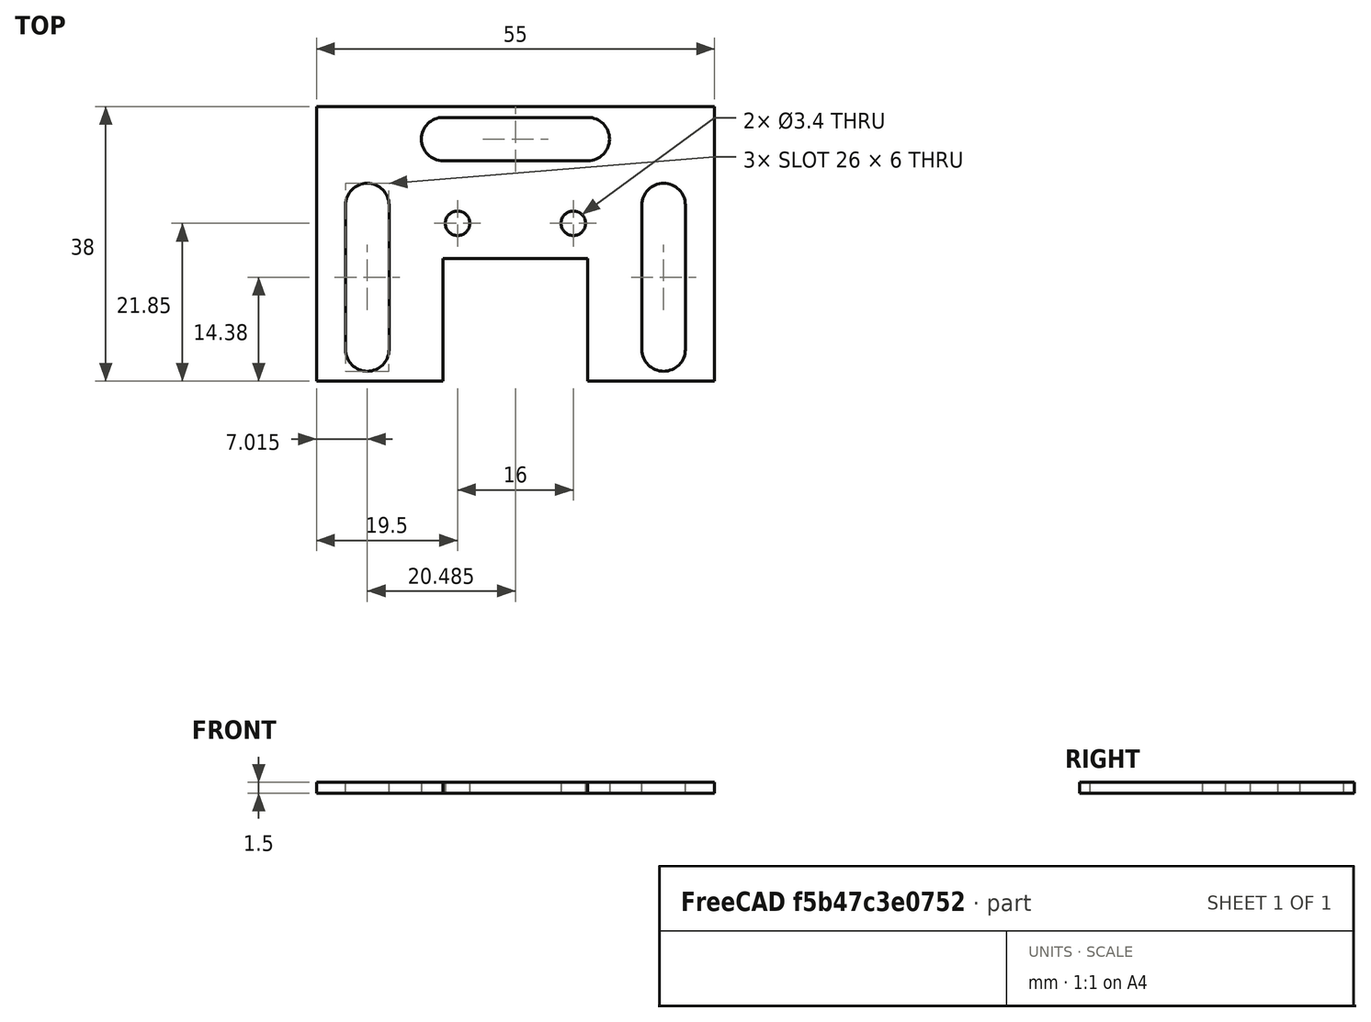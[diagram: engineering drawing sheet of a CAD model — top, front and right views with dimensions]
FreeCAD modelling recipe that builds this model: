
FCSTD DOCUMENT  (FreeCAD 0.18.4R)
Label: magnet_support_fixed_1.01
License: All rights reserved
LicenseURL: http://en.wikipedia.org/wiki/All_rights_reserved
objects: Sketcher::SketchObject×1, PartDesign::Pad×1, PartDesign::Body×1
note: 4 computed .brp shape members not serialized (recipe doc carries the construction recipe); baked Part::Feature solids carry a one-line shape summary decoded from their .brp

FEATURE [Sketcher::SketchObject] Sketch
  MapMode = 5
  Support = -> [XY_Plane]
  sketch-geometry (22):
    g0: LineSegment StartX=-27.5 StartY=19 StartZ=0 EndX=27.5 EndY=19 EndZ=0
    g1: LineSegment StartX=27.5 StartY=19 StartZ=0 EndX=27.5 EndY=-19 EndZ=0
    g2: LineSegment StartX=-27.5 StartY=-19 StartZ=0 EndX=-27.5 EndY=19 EndZ=0
    g3: Circle CenterX=-8 CenterY=2.85 CenterZ=0 NormalX=0 NormalY=0 NormalZ=1 AngleXU=0 Radius=1.7
    g4: Circle CenterX=8 CenterY=2.85 CenterZ=0 NormalX=0 NormalY=0 NormalZ=1 AngleXU=0 Radius=1.7
    g5: LineSegment StartX=-27.5 StartY=-19 StartZ=0 EndX=-10 EndY=-19 EndZ=0
    g6: LineSegment StartX=-10 StartY=-19 StartZ=0 EndX=-10 EndY=-2 EndZ=0
    g7: LineSegment StartX=-10 StartY=-2 StartZ=0 EndX=10 EndY=-2 EndZ=0
    g8: LineSegment StartX=10 StartY=-2 StartZ=0 EndX=10 EndY=-19 EndZ=0
    g9: LineSegment StartX=10 StartY=-19 StartZ=0 EndX=27.5 EndY=-19 EndZ=0
    g10: ArcOfCircle CenterX=-10 CenterY=14.5 CenterZ=0 NormalX=0 NormalY=0 NormalZ=1 AngleXU=0 Radius=3 StartAngle=1.5708 EndAngle=4.71239
    g11: ArcOfCircle CenterX=10 CenterY=14.5 CenterZ=0 NormalX=0 NormalY=0 NormalZ=1 AngleXU=0 Radius=3 StartAngle=4.71239 EndAngle=7.85398
    g12: LineSegment StartX=-10 StartY=11.5 StartZ=0 EndX=10 EndY=11.5 EndZ=0
    g13: LineSegment StartX=-10 StartY=17.5 StartZ=0 EndX=10 EndY=17.5 EndZ=0
    g14: ArcOfCircle CenterX=20.485 CenterY=5.38 CenterZ=0 NormalX=0 NormalY=0 NormalZ=1 AngleXU=0 Radius=3 StartAngle=1e-16 EndAngle=3.14159
    g15: ArcOfCircle CenterX=20.485 CenterY=-14.62 CenterZ=0 NormalX=0 NormalY=0 NormalZ=1 AngleXU=0 Radius=3 StartAngle=3.14159 EndAngle=6.28319
    g16: LineSegment StartX=17.485 StartY=5.38 StartZ=0 EndX=17.485 EndY=-14.62 EndZ=0
    g17: LineSegment StartX=23.485 StartY=5.38 StartZ=0 EndX=23.485 EndY=-14.62 EndZ=0
    g18: ArcOfCircle CenterX=-20.485 CenterY=-14.62 CenterZ=0 NormalX=0 NormalY=0 NormalZ=1 AngleXU=0 Radius=3 StartAngle=3.14159 EndAngle=6.28319
    g19: ArcOfCircle CenterX=-20.485 CenterY=5.38 CenterZ=0 NormalX=0 NormalY=0 NormalZ=1 AngleXU=0 Radius=3 StartAngle=0 EndAngle=3.14159
    g20: LineSegment StartX=-17.485 StartY=-14.62 StartZ=0 EndX=-17.485 EndY=5.38 EndZ=0
    g21: LineSegment StartX=-23.485 StartY=-14.62 StartZ=0 EndX=-23.485 EndY=5.38 EndZ=0
  constraints (54):
    c: Coincident(g0,g1)
    c: Coincident(g2,g0)
    c: Vertical(g1)
    c: DistanceX(g0,g0) = 55
    c: DistanceY(g2,g2) = 38
    c: Symmetric(g0,g0,g-2)
    c: Symmetric(g0,g2,g-1)
    c: Symmetric(g3,g4,g-2)
    c: Distance(g4,g3) = 16
    c: Coincident(g2,g5)
    c: Horizontal(g5)
    c: Coincident(g5,g6)
    c: Vertical(g6)
    c: Coincident(g6,g7)
    c: Coincident(g7,g8)
    c: Coincident(g8,g9)
    c: Coincident(g9,g1)
    c: Horizontal(g9)
    c: Horizontal(g5,g8)
    c: Vertical(g8,g7)
    c: DistanceX(g7,g7) = 20
    c: Symmetric(g6,g7,g-2)
    c: DistanceY(g6,g6) = 17
    c: Tangent(g10,g13) = 1.5708
    c: Tangent(g10,g12) = -1.5708
    c: Tangent(g12,g11) = -1.5708
    c: Tangent(g13,g11) = 1.5708
    c: Horizontal(g12)
    c: Tangent(g14,g17) = 1.5708
    c: Tangent(g14,g16) = -1.5708
    c: Tangent(g16,g15) = -1.5708
    c: Tangent(g17,g15) = 1.5708
    c: Vertical(g16)
    c: Equal(g14,g15)
    c: Tangent(g18,g21) = 1.5708
    c: Tangent(g18,g20) = -1.5708
    c: Tangent(g20,g19) = -1.5708
    c: Tangent(g21,g19) = 1.5708
    c: Vertical(g20)
    c: Equal(g18,g19)
    c: Distance(g19,g18) = 20
    c: Distance(g10,g11) = 20
    c: Distance(g14,g15) = 20
    c: Distance(g10,g10) = 6
    c: Distance(g14,g14) = 6
    c: Distance(g19,g19) = 6
    c: Distance(g19,g14) = 40.97
    c: Symmetric(g14,g19,g-2)
    c: Distance(g3,g12) = 8.65
    c: Symmetric(g10,g11,g-2)
    c: Distance(g19,g12) = 6.12
    c: Distance(g10,g0) = 1.5
    c: Radius(g3) = 1.7
    c: Radius(g4) = 1.7
FEATURE [PartDesign::Pad] Pad
  Length = 1.5
  Length2 = 100
  Profile = -> Sketch
  Type = 0
FEATURE [PartDesign::Body] Body
  Group = -> [Sketch,Pad]
  Origin = -> Origin
  Tip = -> Pad
